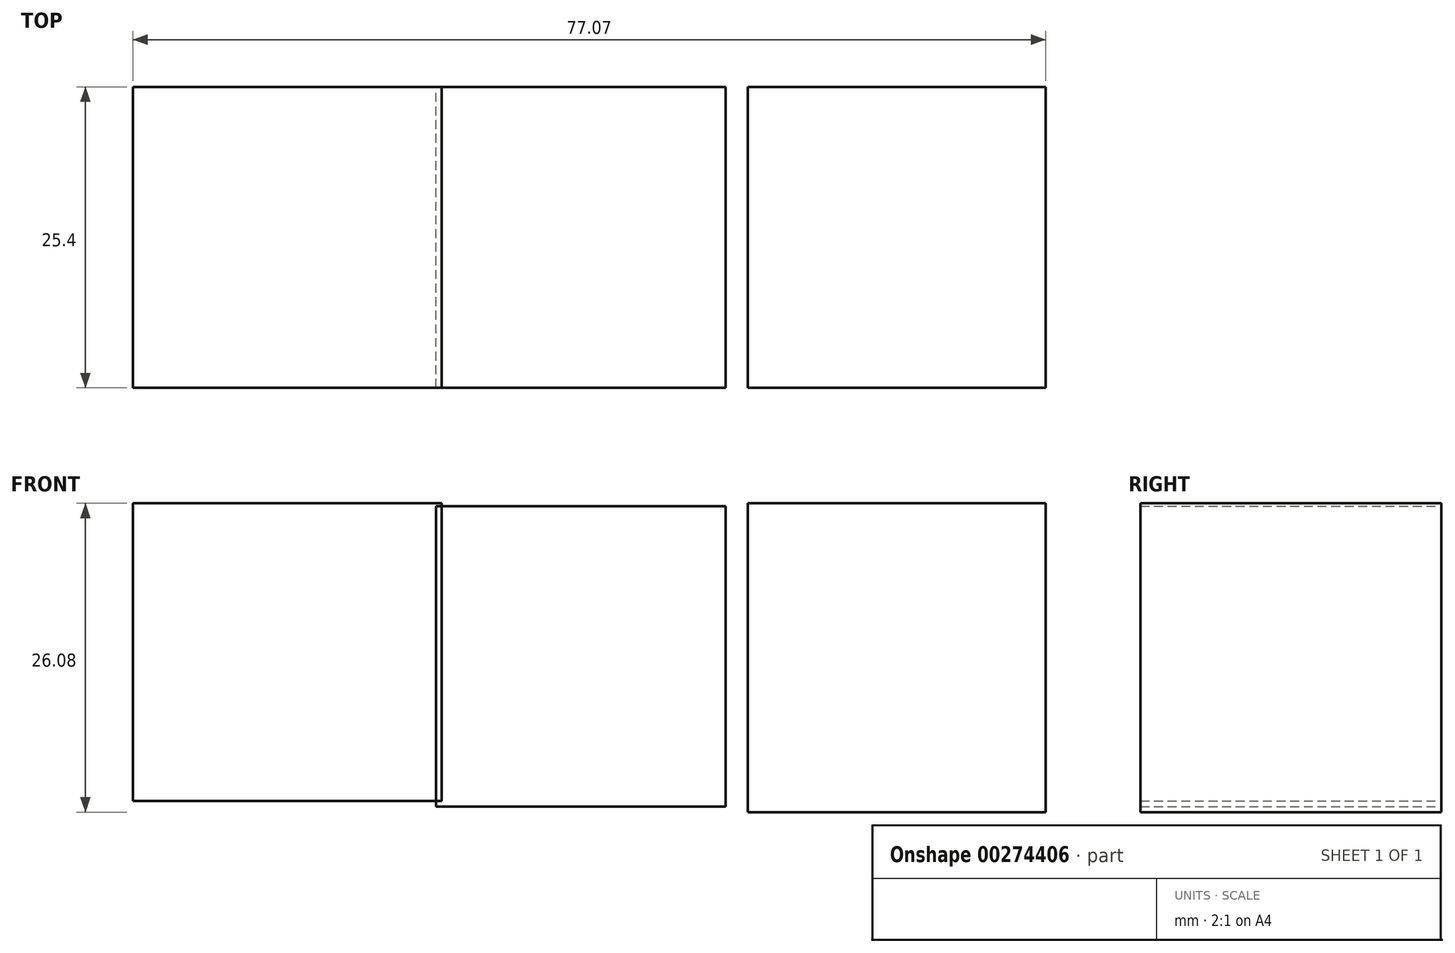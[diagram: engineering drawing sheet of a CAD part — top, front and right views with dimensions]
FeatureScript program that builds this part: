
annotation { "Feature Type Name" : "Feature", "Feature Type Description" : "" }
export const myFeature = defineFeature(function(context is Context, id is Id, definition is map)
    precondition{}
    {
        {
            var Q0;
            Q0=qCreatedBy(makeId("Front.planeOp"),FACE);
            var sketch = newSketch(context, id + "F0", { "sketchPlane" : qUnion([Q0])});
            skLineSegment(sketch, "E0.bottom", {"start": v(-69.32, 65.44) * mm, "end": v(-43.24, 65.44) * mm});
            skLineSegment(sketch, "E0.top", {"start": v(-69.32, 40.3) * mm, "end": v(-43.24, 40.3) * mm});
            skLineSegment(sketch, "E0.left", {"start": v(-69.32, 65.44) * mm, "end": v(-69.32, 40.3) * mm});
            skLineSegment(sketch, "E0.right", {"start": v(-43.24, 65.44) * mm, "end": v(-43.24, 40.3) * mm});
            skSolve(sketch);
        }
        {
            var Q0;
            Q0=qCreatedBy(makeId("Front.planeOp"),FACE);
            var sketch = newSketch(context, id + "F1", { "sketchPlane" : qUnion([Q0])});
            skLineSegment(sketch, "E1.bottom", {"start": v(-43.7, 65.2) * mm, "end": v(-19.27, 65.2) * mm});
            skLineSegment(sketch, "E1.top", {"start": v(-43.7, 39.83) * mm, "end": v(-19.27, 39.83) * mm});
            skLineSegment(sketch, "E1.left", {"start": v(-43.7, 65.2) * mm, "end": v(-43.7, 39.83) * mm});
            skLineSegment(sketch, "E1.right", {"start": v(-19.27, 65.2) * mm, "end": v(-19.27, 39.83) * mm});
            skSolve(sketch);
        }
        {
            var Q0;
            Q0 = qSketchRegion(id + "F0", true);
            var Q1;
            Q1 = qSketchRegion(id + "F1", true);
            extrude(context, id + "F2", {"entities" : qUnion([Q0, Q1]), "depth" : 25.4 * mm});
        }
        {
            var Q0;
            Q0 = qSketchRegion(id + "F1", true);
            extrude(context, id + "F3", {"entities" : qUnion([Q0]), "depth" : 25.4 * mm});
        }
        {
            var Q0;
            Q0=qCreatedBy(makeId("Front.planeOp"),FACE);
            var sketch = newSketch(context, id + "F4", { "sketchPlane" : qUnion([Q0])});
            skLineSegment(sketch, "E2.bottom", {"start": v(-17.39, 65.44) * mm, "end": v(7.75, 65.44) * mm});
            skLineSegment(sketch, "E2.top", {"start": v(-17.39, 39.36) * mm, "end": v(7.75, 39.36) * mm});
            skLineSegment(sketch, "E2.left", {"start": v(-17.39, 65.44) * mm, "end": v(-17.39, 39.36) * mm});
            skLineSegment(sketch, "E2.right", {"start": v(7.75, 65.44) * mm, "end": v(7.75, 39.36) * mm});
            skSolve(sketch);
        }
        {
            var Q0;
            Q0 = qSketchRegion(id + "F4", true);
            extrude(context, id + "F5", {"entities" : qUnion([Q0]), "depth" : 25.4 * mm});
        }
    });
